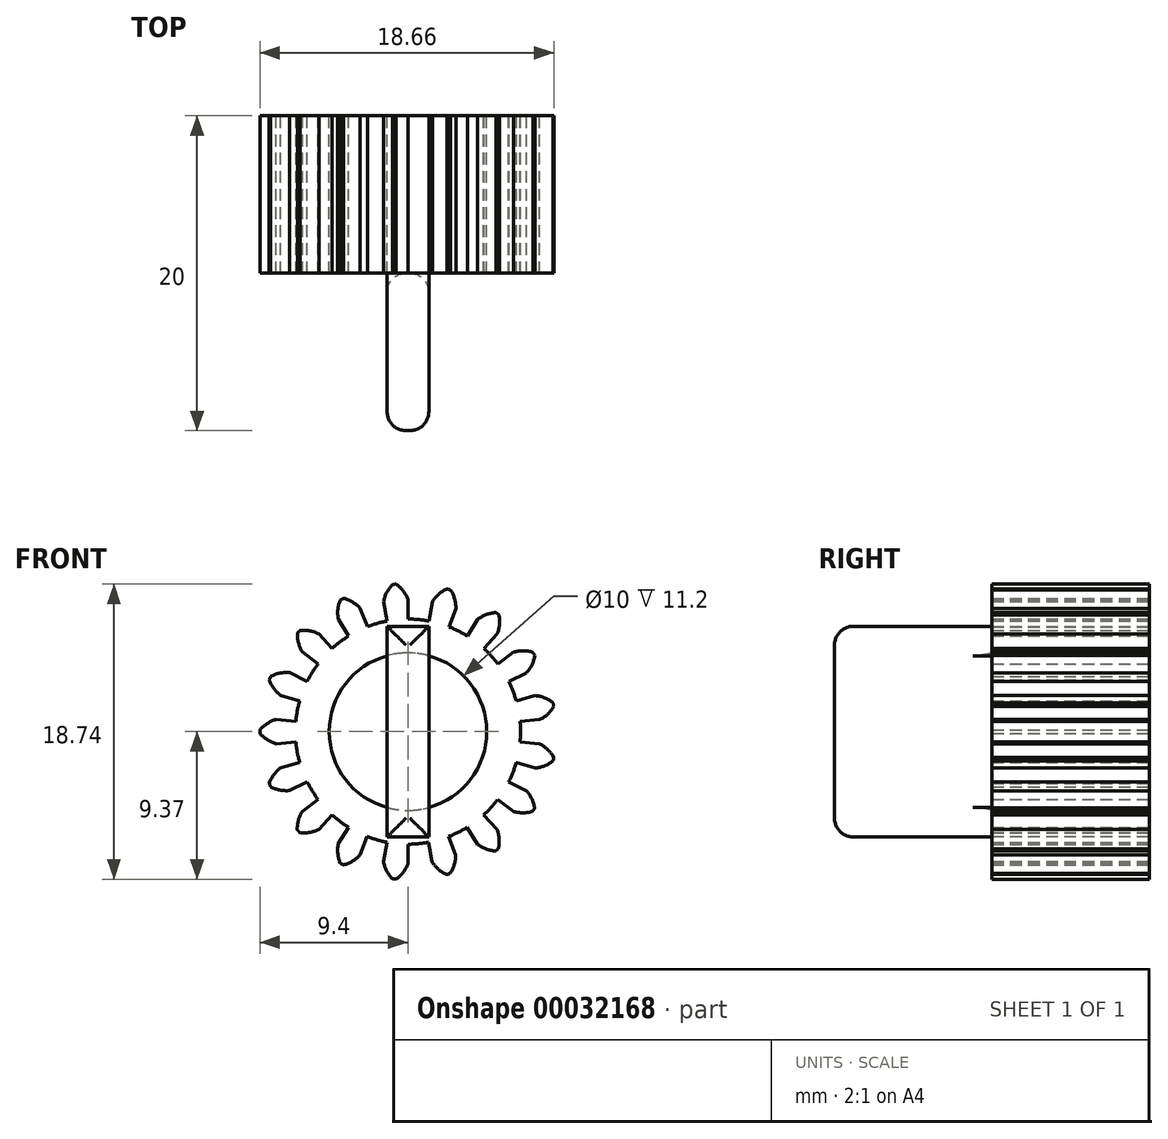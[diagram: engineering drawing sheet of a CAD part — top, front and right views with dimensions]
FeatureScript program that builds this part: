
annotation { "Feature Type Name" : "Feature", "Feature Type Description" : "" }
export const myFeature = defineFeature(function(context is Context, id is Id, definition is map)
    precondition{}
    {
        {
            var Q0;
            Q0=qCreatedBy(makeId("Front.planeOp"),FACE);
            var sketch = newSketch(context, id + "F0", { "sketchPlane" : qUnion([Q0])});
            skArc(sketch, "E0", {"start": v(-0.75, 9.37) * mm, "mid": v(-0.87, 9.36) * mm, "end": v(-0.99, 9.35) * mm});
            skLineSegment(sketch, "E1", {"start": v(0, 7.15) * mm, "end": v(0, 8.4) * mm});
            skArc(sketch, "E2", {"start": v(0, 8.4) * mm, "mid": v(-0.3, 8.94) * mm, "end": v(-0.75, 9.37) * mm});
            skArc(sketch, "E3.0.MirrorCS", {"start": v(-1.55, 8.26) * mm, "mid": v(-1.35, 8.84) * mm, "end": v(-0.99, 9.35) * mm});
            skLineSegment(sketch, "E4.0.MirrorCS", {"start": v(-1.32, 7.03) * mm, "end": v(-1.55, 8.26) * mm});
            skArc(sketch, "E5", {"start": v(-1.32, 7.03) * mm, "mid": v(0.66, -7.12) * mm, "end": v(0, 7.15) * mm});
            skCircle(sketch, "E6", {"center": v(0, 0) * mm, "radius": 5 * mm});
            skSolve(sketch);
        }
        {
            var Q0;
            Q0=makeQuery(id+"F0.imprint","IMPRINT",FACE,{"disambiguationData":[TD([[makeQuery(id+"F0.imprint","IMPRINT",EDGE,{"derivedFrom":sQuery(id+"F0.wireOp",EDGE,"E0")}),1.0]])]});
            var Q1;
            Q1=makeQuery(id+"F0.imprint","IMPRINT",FACE,{"disambiguationData":[TD([[makeQuery(id+"F0.imprint","IMPRINT",EDGE,{"derivedFrom":sQuery(id+"F0.wireOp",EDGE,"E1")}),1.0]])]});
            extrude(context, id + "F1", {"entities" : qUnion([Q0, Q1]), "depth" : 10 * mm});
        }
        {
            var Q0;
            Q0=makeQuery(id+"F1.opExtrude","SWEPT_BODY",BODY,{"disambiguationData":[OSD([sQuery(id+"F0.wireOp",EDGE,"E1"),sQuery(id+"F0.wireOp",EDGE,"E2"),sQuery(id+"F0.wireOp",EDGE,"E3.0.MirrorCS"),sQuery(id+"F0.wireOp",EDGE,"E4.0.MirrorCS"),sQuery(id+"F0.wireOp",EDGE,"E0"),sQuery(id+"F0.wireOp",EDGE,"E5"),sQuery(id+"F0.wireOp",EDGE,"E6")])]});
            var Q1;
            Q1=makeQuery(id+"F1.opExtrude","SWEPT_FACE",FACE,{"disambiguationData":[OSD([sQuery(id+"F0.wireOp",EDGE,"E6")])]});
            circularPattern(context, id + "F2", {"entities" : qUnion([Q0]), "axis" : qUnion([Q1]), "angle" : 21.17 * degree, "instanceCount" : round(17)});
        }
        {
            var Q0;
            Q0=makeQuery(id+"F2.opPattern","COPY",BODY,{"derivedFrom":makeQuery(id+"F1.opExtrude","SWEPT_BODY",BODY,{"disambiguationData":[OSD([sQuery(id+"F0.wireOp",EDGE,"E1"),sQuery(id+"F0.wireOp",EDGE,"E2"),sQuery(id+"F0.wireOp",EDGE,"E3.0.MirrorCS"),sQuery(id+"F0.wireOp",EDGE,"E4.0.MirrorCS"),sQuery(id+"F0.wireOp",EDGE,"E0"),sQuery(id+"F0.wireOp",EDGE,"E5"),sQuery(id+"F0.wireOp",EDGE,"E6")])]}),"instanceName":"7"});
            var Q1;
            Q1=makeQuery(id+"F2.opPattern","COPY",BODY,{"derivedFrom":makeQuery(id+"F1.opExtrude","SWEPT_BODY",BODY,{"disambiguationData":[OSD([sQuery(id+"F0.wireOp",EDGE,"E1"),sQuery(id+"F0.wireOp",EDGE,"E2"),sQuery(id+"F0.wireOp",EDGE,"E3.0.MirrorCS"),sQuery(id+"F0.wireOp",EDGE,"E4.0.MirrorCS"),sQuery(id+"F0.wireOp",EDGE,"E0"),sQuery(id+"F0.wireOp",EDGE,"E5"),sQuery(id+"F0.wireOp",EDGE,"E6")])]}),"instanceName":"15"});
            var Q2;
            Q2=makeQuery(id+"F2.opPattern","COPY",BODY,{"derivedFrom":makeQuery(id+"F1.opExtrude","SWEPT_BODY",BODY,{"disambiguationData":[OSD([sQuery(id+"F0.wireOp",EDGE,"E1"),sQuery(id+"F0.wireOp",EDGE,"E2"),sQuery(id+"F0.wireOp",EDGE,"E3.0.MirrorCS"),sQuery(id+"F0.wireOp",EDGE,"E4.0.MirrorCS"),sQuery(id+"F0.wireOp",EDGE,"E0"),sQuery(id+"F0.wireOp",EDGE,"E5"),sQuery(id+"F0.wireOp",EDGE,"E6")])]}),"instanceName":"16"});
            var Q3;
            Q3=makeQuery(id+"F2.opPattern","COPY",BODY,{"derivedFrom":makeQuery(id+"F1.opExtrude","SWEPT_BODY",BODY,{"disambiguationData":[OSD([sQuery(id+"F0.wireOp",EDGE,"E1"),sQuery(id+"F0.wireOp",EDGE,"E2"),sQuery(id+"F0.wireOp",EDGE,"E3.0.MirrorCS"),sQuery(id+"F0.wireOp",EDGE,"E4.0.MirrorCS"),sQuery(id+"F0.wireOp",EDGE,"E0"),sQuery(id+"F0.wireOp",EDGE,"E5"),sQuery(id+"F0.wireOp",EDGE,"E6")])]}),"instanceName":"1"});
            var Q4;
            Q4=makeQuery(id+"F2.opPattern","COPY",BODY,{"derivedFrom":makeQuery(id+"F1.opExtrude","SWEPT_BODY",BODY,{"disambiguationData":[OSD([sQuery(id+"F0.wireOp",EDGE,"E1"),sQuery(id+"F0.wireOp",EDGE,"E2"),sQuery(id+"F0.wireOp",EDGE,"E3.0.MirrorCS"),sQuery(id+"F0.wireOp",EDGE,"E4.0.MirrorCS"),sQuery(id+"F0.wireOp",EDGE,"E0"),sQuery(id+"F0.wireOp",EDGE,"E5"),sQuery(id+"F0.wireOp",EDGE,"E6")])]}),"instanceName":"5"});
            var Q5;
            Q5=makeQuery(id+"F2.opPattern","COPY",BODY,{"derivedFrom":makeQuery(id+"F1.opExtrude","SWEPT_BODY",BODY,{"disambiguationData":[OSD([sQuery(id+"F0.wireOp",EDGE,"E1"),sQuery(id+"F0.wireOp",EDGE,"E2"),sQuery(id+"F0.wireOp",EDGE,"E3.0.MirrorCS"),sQuery(id+"F0.wireOp",EDGE,"E4.0.MirrorCS"),sQuery(id+"F0.wireOp",EDGE,"E0"),sQuery(id+"F0.wireOp",EDGE,"E5"),sQuery(id+"F0.wireOp",EDGE,"E6")])]}),"instanceName":"9"});
            var Q6;
            Q6=makeQuery(id+"F2.opPattern","COPY",BODY,{"derivedFrom":makeQuery(id+"F1.opExtrude","SWEPT_BODY",BODY,{"disambiguationData":[OSD([sQuery(id+"F0.wireOp",EDGE,"E1"),sQuery(id+"F0.wireOp",EDGE,"E2"),sQuery(id+"F0.wireOp",EDGE,"E3.0.MirrorCS"),sQuery(id+"F0.wireOp",EDGE,"E4.0.MirrorCS"),sQuery(id+"F0.wireOp",EDGE,"E0"),sQuery(id+"F0.wireOp",EDGE,"E5"),sQuery(id+"F0.wireOp",EDGE,"E6")])]}),"instanceName":"3"});
            var Q7;
            Q7=makeQuery(id+"F2.opPattern","COPY",BODY,{"derivedFrom":makeQuery(id+"F1.opExtrude","SWEPT_BODY",BODY,{"disambiguationData":[OSD([sQuery(id+"F0.wireOp",EDGE,"E1"),sQuery(id+"F0.wireOp",EDGE,"E2"),sQuery(id+"F0.wireOp",EDGE,"E3.0.MirrorCS"),sQuery(id+"F0.wireOp",EDGE,"E4.0.MirrorCS"),sQuery(id+"F0.wireOp",EDGE,"E0"),sQuery(id+"F0.wireOp",EDGE,"E5"),sQuery(id+"F0.wireOp",EDGE,"E6")])]}),"instanceName":"12"});
            var Q8;
            Q8=makeQuery(id+"F2.opPattern","COPY",BODY,{"derivedFrom":makeQuery(id+"F1.opExtrude","SWEPT_BODY",BODY,{"disambiguationData":[OSD([sQuery(id+"F0.wireOp",EDGE,"E1"),sQuery(id+"F0.wireOp",EDGE,"E2"),sQuery(id+"F0.wireOp",EDGE,"E3.0.MirrorCS"),sQuery(id+"F0.wireOp",EDGE,"E4.0.MirrorCS"),sQuery(id+"F0.wireOp",EDGE,"E0"),sQuery(id+"F0.wireOp",EDGE,"E5"),sQuery(id+"F0.wireOp",EDGE,"E6")])]}),"instanceName":"4"});
            var Q9;
            Q9=makeQuery(id+"F2.opPattern","COPY",BODY,{"derivedFrom":makeQuery(id+"F1.opExtrude","SWEPT_BODY",BODY,{"disambiguationData":[OSD([sQuery(id+"F0.wireOp",EDGE,"E1"),sQuery(id+"F0.wireOp",EDGE,"E2"),sQuery(id+"F0.wireOp",EDGE,"E3.0.MirrorCS"),sQuery(id+"F0.wireOp",EDGE,"E4.0.MirrorCS"),sQuery(id+"F0.wireOp",EDGE,"E0"),sQuery(id+"F0.wireOp",EDGE,"E5"),sQuery(id+"F0.wireOp",EDGE,"E6")])]}),"instanceName":"11"});
            var Q10;
            Q10=makeQuery(id+"F2.opPattern","COPY",BODY,{"derivedFrom":makeQuery(id+"F1.opExtrude","SWEPT_BODY",BODY,{"disambiguationData":[OSD([sQuery(id+"F0.wireOp",EDGE,"E1"),sQuery(id+"F0.wireOp",EDGE,"E2"),sQuery(id+"F0.wireOp",EDGE,"E3.0.MirrorCS"),sQuery(id+"F0.wireOp",EDGE,"E4.0.MirrorCS"),sQuery(id+"F0.wireOp",EDGE,"E0"),sQuery(id+"F0.wireOp",EDGE,"E5"),sQuery(id+"F0.wireOp",EDGE,"E6")])]}),"instanceName":"10"});
            var Q11;
            Q11=makeQuery(id+"F2.opPattern","COPY",BODY,{"derivedFrom":makeQuery(id+"F1.opExtrude","SWEPT_BODY",BODY,{"disambiguationData":[OSD([sQuery(id+"F0.wireOp",EDGE,"E1"),sQuery(id+"F0.wireOp",EDGE,"E2"),sQuery(id+"F0.wireOp",EDGE,"E3.0.MirrorCS"),sQuery(id+"F0.wireOp",EDGE,"E4.0.MirrorCS"),sQuery(id+"F0.wireOp",EDGE,"E0"),sQuery(id+"F0.wireOp",EDGE,"E5"),sQuery(id+"F0.wireOp",EDGE,"E6")])]}),"instanceName":"2"});
            var Q12;
            Q12=makeQuery(id+"F2.opPattern","COPY",BODY,{"derivedFrom":makeQuery(id+"F1.opExtrude","SWEPT_BODY",BODY,{"disambiguationData":[OSD([sQuery(id+"F0.wireOp",EDGE,"E1"),sQuery(id+"F0.wireOp",EDGE,"E2"),sQuery(id+"F0.wireOp",EDGE,"E3.0.MirrorCS"),sQuery(id+"F0.wireOp",EDGE,"E4.0.MirrorCS"),sQuery(id+"F0.wireOp",EDGE,"E0"),sQuery(id+"F0.wireOp",EDGE,"E5"),sQuery(id+"F0.wireOp",EDGE,"E6")])]}),"instanceName":"6"});
            var Q13;
            Q13=makeQuery(id+"F2.opPattern","COPY",BODY,{"derivedFrom":makeQuery(id+"F1.opExtrude","SWEPT_BODY",BODY,{"disambiguationData":[OSD([sQuery(id+"F0.wireOp",EDGE,"E1"),sQuery(id+"F0.wireOp",EDGE,"E2"),sQuery(id+"F0.wireOp",EDGE,"E3.0.MirrorCS"),sQuery(id+"F0.wireOp",EDGE,"E4.0.MirrorCS"),sQuery(id+"F0.wireOp",EDGE,"E0"),sQuery(id+"F0.wireOp",EDGE,"E5"),sQuery(id+"F0.wireOp",EDGE,"E6")])]}),"instanceName":"8"});
            var Q14;
            Q14=makeQuery(id+"F2.opPattern","COPY",BODY,{"derivedFrom":makeQuery(id+"F1.opExtrude","SWEPT_BODY",BODY,{"disambiguationData":[OSD([sQuery(id+"F0.wireOp",EDGE,"E1"),sQuery(id+"F0.wireOp",EDGE,"E2"),sQuery(id+"F0.wireOp",EDGE,"E3.0.MirrorCS"),sQuery(id+"F0.wireOp",EDGE,"E4.0.MirrorCS"),sQuery(id+"F0.wireOp",EDGE,"E0"),sQuery(id+"F0.wireOp",EDGE,"E5"),sQuery(id+"F0.wireOp",EDGE,"E6")])]}),"instanceName":"13"});
            var Q15;
            Q15=makeQuery(id+"F2.opPattern","COPY",BODY,{"derivedFrom":makeQuery(id+"F1.opExtrude","SWEPT_BODY",BODY,{"disambiguationData":[OSD([sQuery(id+"F0.wireOp",EDGE,"E1"),sQuery(id+"F0.wireOp",EDGE,"E2"),sQuery(id+"F0.wireOp",EDGE,"E3.0.MirrorCS"),sQuery(id+"F0.wireOp",EDGE,"E4.0.MirrorCS"),sQuery(id+"F0.wireOp",EDGE,"E0"),sQuery(id+"F0.wireOp",EDGE,"E5"),sQuery(id+"F0.wireOp",EDGE,"E6")])]}),"instanceName":"14"});
            var Q16;
            Q16=makeQuery(id+"F1.opExtrude","SWEPT_BODY",BODY,{"disambiguationData":[OSD([sQuery(id+"F0.wireOp",EDGE,"E1"),sQuery(id+"F0.wireOp",EDGE,"E2"),sQuery(id+"F0.wireOp",EDGE,"E3.0.MirrorCS"),sQuery(id+"F0.wireOp",EDGE,"E4.0.MirrorCS"),sQuery(id+"F0.wireOp",EDGE,"E0"),sQuery(id+"F0.wireOp",EDGE,"E5"),sQuery(id+"F0.wireOp",EDGE,"E6")])]});
            booleanBodies(context, id + "F3", {"operationType" : BooleanOperationType.UNION, "tools" : qUnion([Q0, Q1, Q2, Q3, Q4, Q5, Q6, Q7, Q8, Q9, Q10, Q11, Q12, Q13, Q14, Q15, Q16])});
        }
        {
            var Q0;
            {var subQ0=makeQuery(id+"F1.opExtrude","CAP_FACE",FACE,{"disambiguationData":[OSD([sQuery(id+"F0.wireOp",EDGE,"E1"),sQuery(id+"F0.wireOp",EDGE,"E2"),sQuery(id+"F0.wireOp",EDGE,"E3.0.MirrorCS"),sQuery(id+"F0.wireOp",EDGE,"E4.0.MirrorCS"),sQuery(id+"F0.wireOp",EDGE,"E0"),sQuery(id+"F0.wireOp",EDGE,"E5"),sQuery(id+"F0.wireOp",EDGE,"E6")])],"isStart":false});Q0=makeQuery(id+"F3.opBoolean","MERGE",FACE,{"derivedFrom":[subQ0,makeQuery(id+"F2.opPattern","COPY",FACE,{"derivedFrom":subQ0,"instanceName":"1"}),makeQuery(id+"F2.opPattern","COPY",FACE,{"derivedFrom":subQ0,"instanceName":"2"}),makeQuery(id+"F2.opPattern","COPY",FACE,{"derivedFrom":subQ0,"instanceName":"3"}),makeQuery(id+"F2.opPattern","COPY",FACE,{"derivedFrom":subQ0,"instanceName":"4"}),makeQuery(id+"F2.opPattern","COPY",FACE,{"derivedFrom":subQ0,"instanceName":"5"}),makeQuery(id+"F2.opPattern","COPY",FACE,{"derivedFrom":subQ0,"instanceName":"6"}),makeQuery(id+"F2.opPattern","COPY",FACE,{"derivedFrom":subQ0,"instanceName":"7"}),makeQuery(id+"F2.opPattern","COPY",FACE,{"derivedFrom":subQ0,"instanceName":"8"}),makeQuery(id+"F2.opPattern","COPY",FACE,{"derivedFrom":subQ0,"instanceName":"9"}),makeQuery(id+"F2.opPattern","COPY",FACE,{"derivedFrom":subQ0,"instanceName":"10"}),makeQuery(id+"F2.opPattern","COPY",FACE,{"derivedFrom":subQ0,"instanceName":"11"}),makeQuery(id+"F2.opPattern","COPY",FACE,{"derivedFrom":subQ0,"instanceName":"12"}),makeQuery(id+"F2.opPattern","COPY",FACE,{"derivedFrom":subQ0,"instanceName":"13"}),makeQuery(id+"F2.opPattern","COPY",FACE,{"derivedFrom":subQ0,"instanceName":"14"}),makeQuery(id+"F2.opPattern","COPY",FACE,{"derivedFrom":subQ0,"instanceName":"15"}),makeQuery(id+"F2.opPattern","COPY",FACE,{"derivedFrom":subQ0,"instanceName":"16"})]});}
            var sketch = newSketch(context, id + "F4", { "sketchPlane" : qUnion([Q0])});
            skLineSegment(sketch, "E7.rect.bottom", {"start": v(1.32, 6.7) * mm, "end": v(-1.32, 6.7) * mm});
            skLineSegment(sketch, "E7.rect.top", {"start": v(1.32, -6.7) * mm, "end": v(-1.32, -6.7) * mm});
            skLineSegment(sketch, "E7.rect.left", {"start": v(1.32, 6.7) * mm, "end": v(1.32, -6.7) * mm});
            skLineSegment(sketch, "E7.rect.right", {"start": v(-1.32, 6.7) * mm, "end": v(-1.32, -6.7) * mm});
            skPoint(sketch, "E7.rect.middle", {"position": v(0, 0) * mm});
            skSolve(sketch);
        }
        {
            var Q0;
            {var subQ5=sQuery(id+"F4.wireOp",EDGE,"E7.rect.bottom");Q0=makeQuery(id+"F4.imprint","IMPRINT",FACE,{"disambiguationData":[TD([[makeQuery(id+"F4.imprint","IMPRINT",EDGE,{"derivedFrom":subQ5}),1.0]])]});}
            var Q1;
            {var subQ0=makeQuery(id+"F2.opPattern","COPY",EDGE,{"derivedFrom":makeQuery(id+"F1.opExtrude","CAP_EDGE",EDGE,{"disambiguationData":[OSD([sQuery(id+"F0.wireOp",EDGE,"E6")])],"isStart":false}),"instanceName":"7"});var subQ3=sQuery(id+"F4.wireOp",EDGE,"E7.rect.left");var subQ4=makeQuery(id+"F4.imprint","INTERSECT",VERTEX,{"disambiguationData":[OD(0.0)],"derivedFrom":[subQ0,subQ3]});Q1=makeQuery(id+"F4.imprint","IMPRINT",FACE,{"disambiguationData":[TD([[makeQuery(id+"F4.imprint","IMPRINT",EDGE,{"disambiguationData":[TD([[subQ4,-1.0]])],"derivedFrom":subQ3}),-1.0]])]});}
            var Q2;
            {var subQ5=sQuery(id+"F4.wireOp",EDGE,"E7.rect.top");Q2=makeQuery(id+"F4.imprint","IMPRINT",FACE,{"disambiguationData":[TD([[makeQuery(id+"F4.imprint","IMPRINT",EDGE,{"derivedFrom":subQ5}),-1.0]])]});}
            extrude(context, id + "F5", {"entities" : qUnion([Q0, Q1, Q2]), "operationType" : NewBodyOperationType.ADD, "depth" : 10 * mm});
        }
        {
            var Q0;
            {var subQ0=sQuery(id+"F4.wireOp",EDGE,"E7.rect.right");var subQ1=sQuery(id+"F4.wireOp",EDGE,"E7.rect.bottom");var subQ2=sQuery(id+"F0.wireOp",EDGE,"E6");var subQ3=makeQuery(id+"F1.opExtrude","CAP_FACE",FACE,{"disambiguationData":[OSD([sQuery(id+"F0.wireOp",EDGE,"E1"),sQuery(id+"F0.wireOp",EDGE,"E2"),sQuery(id+"F0.wireOp",EDGE,"E3.0.MirrorCS"),sQuery(id+"F0.wireOp",EDGE,"E4.0.MirrorCS"),sQuery(id+"F0.wireOp",EDGE,"E0"),sQuery(id+"F0.wireOp",EDGE,"E5"),subQ2])],"isStart":false});Q0=makeQuery(id+"F5.boolean.opBoolean","SPLIT",EDGE,{"disambiguationData":[TD([subQ3,makeQuery(id+"F2.opPattern","COPY",FACE,{"derivedFrom":subQ3,"instanceName":"1"}),makeQuery(id+"F2.opPattern","COPY",FACE,{"derivedFrom":subQ3,"instanceName":"2"}),makeQuery(id+"F2.opPattern","COPY",FACE,{"derivedFrom":subQ3,"instanceName":"3"}),makeQuery(id+"F2.opPattern","COPY",FACE,{"derivedFrom":subQ3,"instanceName":"4"}),makeQuery(id+"F2.opPattern","COPY",FACE,{"derivedFrom":subQ3,"instanceName":"5"}),makeQuery(id+"F2.opPattern","COPY",FACE,{"derivedFrom":subQ3,"instanceName":"6"}),makeQuery(id+"F2.opPattern","COPY",FACE,{"derivedFrom":subQ3,"instanceName":"7"}),makeQuery(id+"F2.opPattern","COPY",FACE,{"derivedFrom":makeQuery(id+"F1.opExtrude","SWEPT_FACE",FACE,{"disambiguationData":[OSD([subQ2])]}),"instanceName":"7"}),makeQuery(id+"F2.opPattern","COPY",FACE,{"derivedFrom":subQ3,"instanceName":"8"}),makeQuery(id+"F2.opPattern","COPY",FACE,{"derivedFrom":subQ3,"instanceName":"9"}),makeQuery(id+"F2.opPattern","COPY",FACE,{"derivedFrom":subQ3,"instanceName":"10"}),makeQuery(id+"F2.opPattern","COPY",FACE,{"derivedFrom":subQ3,"instanceName":"11"}),makeQuery(id+"F2.opPattern","COPY",FACE,{"derivedFrom":subQ3,"instanceName":"12"}),makeQuery(id+"F2.opPattern","COPY",FACE,{"derivedFrom":subQ3,"instanceName":"13"}),makeQuery(id+"F2.opPattern","COPY",FACE,{"derivedFrom":subQ3,"instanceName":"14"}),makeQuery(id+"F2.opPattern","COPY",FACE,{"derivedFrom":subQ3,"instanceName":"15"}),makeQuery(id+"F2.opPattern","COPY",FACE,{"derivedFrom":subQ3,"instanceName":"16"}),makeQuery(id+"F5.opExtrude","SWEPT_FACE",FACE,{"disambiguationData":[OSD([subQ1])]}),makeQuery(id+"F5.opExtrude","CAP_FACE",FACE,{"disambiguationData":[OSD([subQ1,sQuery(id+"F4.wireOp",EDGE,"E7.rect.top"),sQuery(id+"F4.wireOp",EDGE,"E7.rect.left"),subQ0])],"isStart":true}),makeQuery(id+"F5.opExtrude","SWEPT_FACE",FACE,{"disambiguationData":[OSD([subQ0])]})])],"derivedFrom":makeQuery(id+"F5.opExtrude","CAP_EDGE",EDGE,{"disambiguationData":[OSD([subQ0])],"isStart":true})});}
            var Q1;
            {var subQ0=sQuery(id+"F4.wireOp",EDGE,"E7.rect.right");var subQ1=sQuery(id+"F4.wireOp",EDGE,"E7.rect.top");var subQ2=sQuery(id+"F0.wireOp",EDGE,"E6");var subQ3=makeQuery(id+"F1.opExtrude","CAP_FACE",FACE,{"disambiguationData":[OSD([sQuery(id+"F0.wireOp",EDGE,"E1"),sQuery(id+"F0.wireOp",EDGE,"E2"),sQuery(id+"F0.wireOp",EDGE,"E3.0.MirrorCS"),sQuery(id+"F0.wireOp",EDGE,"E4.0.MirrorCS"),sQuery(id+"F0.wireOp",EDGE,"E0"),sQuery(id+"F0.wireOp",EDGE,"E5"),subQ2])],"isStart":false});Q1=makeQuery(id+"F5.boolean.opBoolean","SPLIT",EDGE,{"disambiguationData":[TD([subQ3,makeQuery(id+"F2.opPattern","COPY",FACE,{"derivedFrom":subQ3,"instanceName":"1"}),makeQuery(id+"F2.opPattern","COPY",FACE,{"derivedFrom":subQ3,"instanceName":"2"}),makeQuery(id+"F2.opPattern","COPY",FACE,{"derivedFrom":subQ3,"instanceName":"3"}),makeQuery(id+"F2.opPattern","COPY",FACE,{"derivedFrom":subQ3,"instanceName":"4"}),makeQuery(id+"F2.opPattern","COPY",FACE,{"derivedFrom":subQ3,"instanceName":"5"}),makeQuery(id+"F2.opPattern","COPY",FACE,{"derivedFrom":subQ3,"instanceName":"6"}),makeQuery(id+"F2.opPattern","COPY",FACE,{"derivedFrom":subQ3,"instanceName":"7"}),makeQuery(id+"F2.opPattern","COPY",FACE,{"derivedFrom":makeQuery(id+"F1.opExtrude","SWEPT_FACE",FACE,{"disambiguationData":[OSD([subQ2])]}),"instanceName":"7"}),makeQuery(id+"F2.opPattern","COPY",FACE,{"derivedFrom":subQ3,"instanceName":"8"}),makeQuery(id+"F2.opPattern","COPY",FACE,{"derivedFrom":subQ3,"instanceName":"9"}),makeQuery(id+"F2.opPattern","COPY",FACE,{"derivedFrom":subQ3,"instanceName":"10"}),makeQuery(id+"F2.opPattern","COPY",FACE,{"derivedFrom":subQ3,"instanceName":"11"}),makeQuery(id+"F2.opPattern","COPY",FACE,{"derivedFrom":subQ3,"instanceName":"12"}),makeQuery(id+"F2.opPattern","COPY",FACE,{"derivedFrom":subQ3,"instanceName":"13"}),makeQuery(id+"F2.opPattern","COPY",FACE,{"derivedFrom":subQ3,"instanceName":"14"}),makeQuery(id+"F2.opPattern","COPY",FACE,{"derivedFrom":subQ3,"instanceName":"15"}),makeQuery(id+"F2.opPattern","COPY",FACE,{"derivedFrom":subQ3,"instanceName":"16"}),makeQuery(id+"F5.opExtrude","CAP_FACE",FACE,{"disambiguationData":[OSD([sQuery(id+"F4.wireOp",EDGE,"E7.rect.bottom"),subQ1,sQuery(id+"F4.wireOp",EDGE,"E7.rect.left"),subQ0])],"isStart":true}),makeQuery(id+"F5.opExtrude","SWEPT_FACE",FACE,{"disambiguationData":[OSD([subQ1])]}),makeQuery(id+"F5.opExtrude","SWEPT_FACE",FACE,{"disambiguationData":[OSD([subQ0])]})])],"derivedFrom":makeQuery(id+"F5.opExtrude","CAP_EDGE",EDGE,{"disambiguationData":[OSD([subQ0])],"isStart":true})});}
            var Q2;
            Q2=makeQuery(id+"F5.opExtrude","CAP_EDGE",EDGE,{"disambiguationData":[OSD([sQuery(id+"F4.wireOp",EDGE,"E7.rect.bottom")])],"isStart":true});
            var Q3;
            {var subQ0=sQuery(id+"F4.wireOp",EDGE,"E7.rect.left");var subQ1=sQuery(id+"F4.wireOp",EDGE,"E7.rect.bottom");var subQ2=sQuery(id+"F0.wireOp",EDGE,"E6");var subQ3=makeQuery(id+"F1.opExtrude","CAP_FACE",FACE,{"disambiguationData":[OSD([sQuery(id+"F0.wireOp",EDGE,"E1"),sQuery(id+"F0.wireOp",EDGE,"E2"),sQuery(id+"F0.wireOp",EDGE,"E3.0.MirrorCS"),sQuery(id+"F0.wireOp",EDGE,"E4.0.MirrorCS"),sQuery(id+"F0.wireOp",EDGE,"E0"),sQuery(id+"F0.wireOp",EDGE,"E5"),subQ2])],"isStart":false});Q3=makeQuery(id+"F5.boolean.opBoolean","SPLIT",EDGE,{"disambiguationData":[TD([subQ3,makeQuery(id+"F2.opPattern","COPY",FACE,{"derivedFrom":subQ3,"instanceName":"1"}),makeQuery(id+"F2.opPattern","COPY",FACE,{"derivedFrom":subQ3,"instanceName":"2"}),makeQuery(id+"F2.opPattern","COPY",FACE,{"derivedFrom":subQ3,"instanceName":"3"}),makeQuery(id+"F2.opPattern","COPY",FACE,{"derivedFrom":subQ3,"instanceName":"4"}),makeQuery(id+"F2.opPattern","COPY",FACE,{"derivedFrom":subQ3,"instanceName":"5"}),makeQuery(id+"F2.opPattern","COPY",FACE,{"derivedFrom":subQ3,"instanceName":"6"}),makeQuery(id+"F2.opPattern","COPY",FACE,{"derivedFrom":subQ3,"instanceName":"7"}),makeQuery(id+"F2.opPattern","COPY",FACE,{"derivedFrom":makeQuery(id+"F1.opExtrude","SWEPT_FACE",FACE,{"disambiguationData":[OSD([subQ2])]}),"instanceName":"7"}),makeQuery(id+"F2.opPattern","COPY",FACE,{"derivedFrom":subQ3,"instanceName":"8"}),makeQuery(id+"F2.opPattern","COPY",FACE,{"derivedFrom":subQ3,"instanceName":"9"}),makeQuery(id+"F2.opPattern","COPY",FACE,{"derivedFrom":subQ3,"instanceName":"10"}),makeQuery(id+"F2.opPattern","COPY",FACE,{"derivedFrom":subQ3,"instanceName":"11"}),makeQuery(id+"F2.opPattern","COPY",FACE,{"derivedFrom":subQ3,"instanceName":"12"}),makeQuery(id+"F2.opPattern","COPY",FACE,{"derivedFrom":subQ3,"instanceName":"13"}),makeQuery(id+"F2.opPattern","COPY",FACE,{"derivedFrom":subQ3,"instanceName":"14"}),makeQuery(id+"F2.opPattern","COPY",FACE,{"derivedFrom":subQ3,"instanceName":"15"}),makeQuery(id+"F2.opPattern","COPY",FACE,{"derivedFrom":subQ3,"instanceName":"16"}),makeQuery(id+"F5.opExtrude","SWEPT_FACE",FACE,{"disambiguationData":[OSD([subQ1])]}),makeQuery(id+"F5.opExtrude","CAP_FACE",FACE,{"disambiguationData":[OSD([subQ1,sQuery(id+"F4.wireOp",EDGE,"E7.rect.top"),subQ0,sQuery(id+"F4.wireOp",EDGE,"E7.rect.right")])],"isStart":true}),makeQuery(id+"F5.opExtrude","SWEPT_FACE",FACE,{"disambiguationData":[OSD([subQ0])]})])],"derivedFrom":makeQuery(id+"F5.opExtrude","CAP_EDGE",EDGE,{"disambiguationData":[OSD([subQ0])],"isStart":true})});}
            var Q4;
            {var subQ0=sQuery(id+"F4.wireOp",EDGE,"E7.rect.left");var subQ1=sQuery(id+"F4.wireOp",EDGE,"E7.rect.top");var subQ2=sQuery(id+"F0.wireOp",EDGE,"E6");var subQ3=makeQuery(id+"F1.opExtrude","CAP_FACE",FACE,{"disambiguationData":[OSD([sQuery(id+"F0.wireOp",EDGE,"E1"),sQuery(id+"F0.wireOp",EDGE,"E2"),sQuery(id+"F0.wireOp",EDGE,"E3.0.MirrorCS"),sQuery(id+"F0.wireOp",EDGE,"E4.0.MirrorCS"),sQuery(id+"F0.wireOp",EDGE,"E0"),sQuery(id+"F0.wireOp",EDGE,"E5"),subQ2])],"isStart":false});Q4=makeQuery(id+"F5.boolean.opBoolean","SPLIT",EDGE,{"disambiguationData":[TD([subQ3,makeQuery(id+"F2.opPattern","COPY",FACE,{"derivedFrom":subQ3,"instanceName":"1"}),makeQuery(id+"F2.opPattern","COPY",FACE,{"derivedFrom":subQ3,"instanceName":"2"}),makeQuery(id+"F2.opPattern","COPY",FACE,{"derivedFrom":subQ3,"instanceName":"3"}),makeQuery(id+"F2.opPattern","COPY",FACE,{"derivedFrom":subQ3,"instanceName":"4"}),makeQuery(id+"F2.opPattern","COPY",FACE,{"derivedFrom":subQ3,"instanceName":"5"}),makeQuery(id+"F2.opPattern","COPY",FACE,{"derivedFrom":subQ3,"instanceName":"6"}),makeQuery(id+"F2.opPattern","COPY",FACE,{"derivedFrom":subQ3,"instanceName":"7"}),makeQuery(id+"F2.opPattern","COPY",FACE,{"derivedFrom":makeQuery(id+"F1.opExtrude","SWEPT_FACE",FACE,{"disambiguationData":[OSD([subQ2])]}),"instanceName":"7"}),makeQuery(id+"F2.opPattern","COPY",FACE,{"derivedFrom":subQ3,"instanceName":"8"}),makeQuery(id+"F2.opPattern","COPY",FACE,{"derivedFrom":subQ3,"instanceName":"9"}),makeQuery(id+"F2.opPattern","COPY",FACE,{"derivedFrom":subQ3,"instanceName":"10"}),makeQuery(id+"F2.opPattern","COPY",FACE,{"derivedFrom":subQ3,"instanceName":"11"}),makeQuery(id+"F2.opPattern","COPY",FACE,{"derivedFrom":subQ3,"instanceName":"12"}),makeQuery(id+"F2.opPattern","COPY",FACE,{"derivedFrom":subQ3,"instanceName":"13"}),makeQuery(id+"F2.opPattern","COPY",FACE,{"derivedFrom":subQ3,"instanceName":"14"}),makeQuery(id+"F2.opPattern","COPY",FACE,{"derivedFrom":subQ3,"instanceName":"15"}),makeQuery(id+"F2.opPattern","COPY",FACE,{"derivedFrom":subQ3,"instanceName":"16"}),makeQuery(id+"F5.opExtrude","CAP_FACE",FACE,{"disambiguationData":[OSD([sQuery(id+"F4.wireOp",EDGE,"E7.rect.bottom"),subQ1,subQ0,sQuery(id+"F4.wireOp",EDGE,"E7.rect.right")])],"isStart":true}),makeQuery(id+"F5.opExtrude","SWEPT_FACE",FACE,{"disambiguationData":[OSD([subQ1])]}),makeQuery(id+"F5.opExtrude","SWEPT_FACE",FACE,{"disambiguationData":[OSD([subQ0])]})])],"derivedFrom":makeQuery(id+"F5.opExtrude","CAP_EDGE",EDGE,{"disambiguationData":[OSD([subQ0])],"isStart":true})});}
            var Q5;
            Q5=makeQuery(id+"F5.opExtrude","CAP_EDGE",EDGE,{"disambiguationData":[OSD([sQuery(id+"F4.wireOp",EDGE,"E7.rect.top")])],"isStart":true});
            var Q6;
            Q6=makeQuery(id+"F5.opExtrude","CAP_FACE",FACE,{"disambiguationData":[OSD([sQuery(id+"F4.wireOp",EDGE,"E7.rect.bottom"),sQuery(id+"F4.wireOp",EDGE,"E7.rect.top"),sQuery(id+"F4.wireOp",EDGE,"E7.rect.left"),sQuery(id+"F4.wireOp",EDGE,"E7.rect.right")])],"isStart":false});
            fillet(context, id + "F6", {"entities" : qUnion([Q0, Q1, Q2, Q3, Q4, Q5, Q6]), "radius" : 1.2 * mm, "tangentPropagation" : true, "allowEdgeOverflow" : false});
        }
    });
